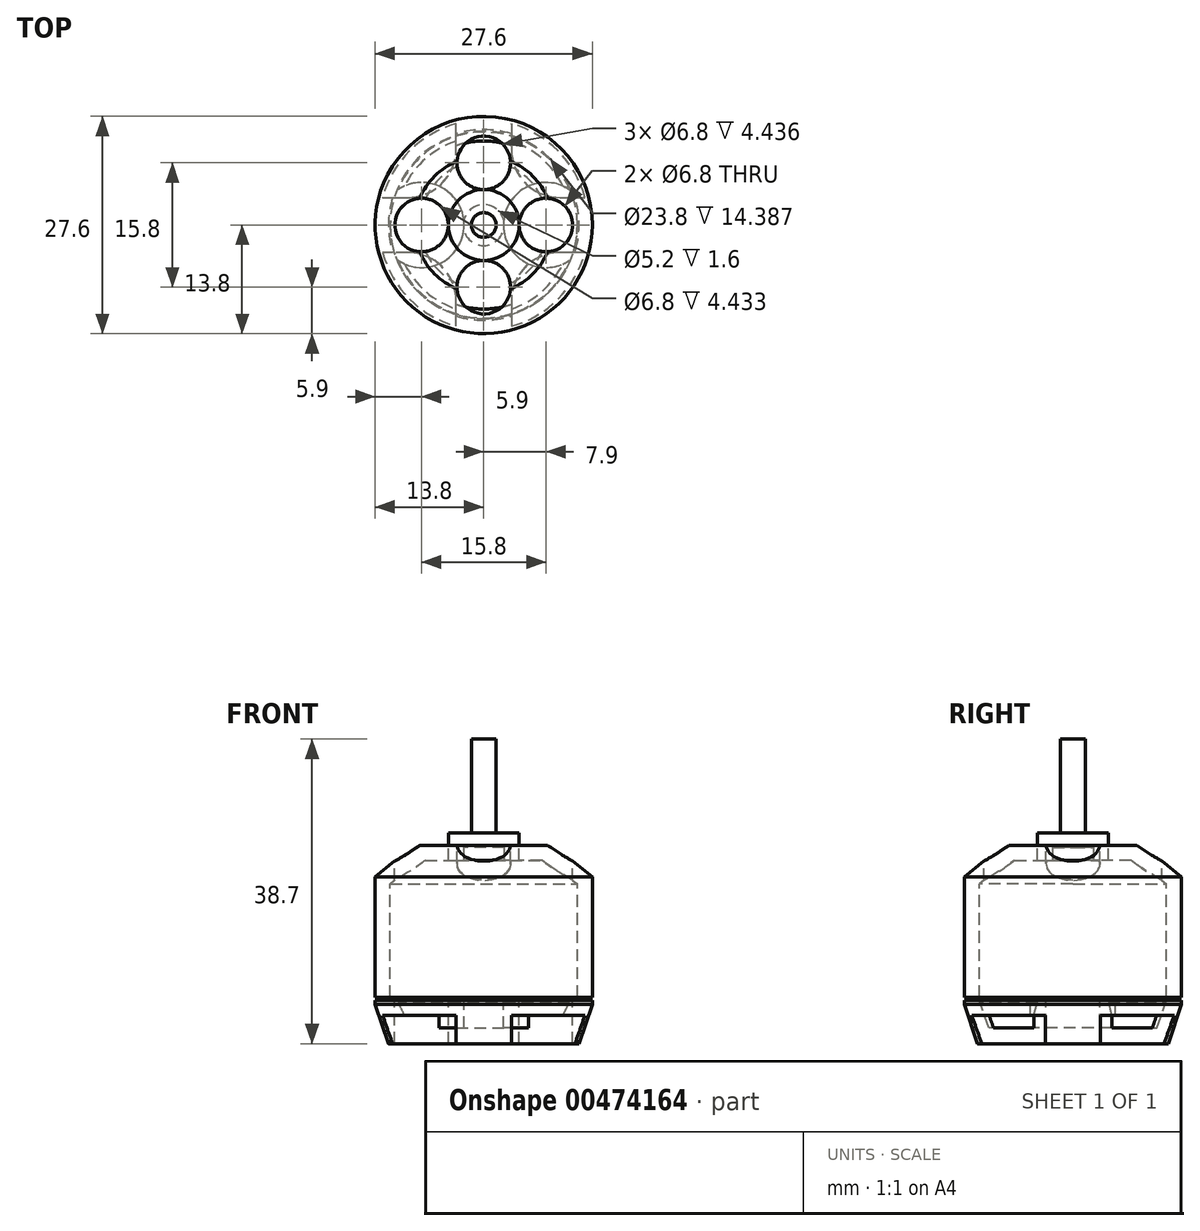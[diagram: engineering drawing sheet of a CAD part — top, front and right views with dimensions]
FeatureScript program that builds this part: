
annotation { "Feature Type Name" : "Feature", "Feature Type Description" : "" }
export const myFeature = defineFeature(function(context is Context, id is Id, definition is map)
    precondition{}
    {
        {
            var Q0;
            Q0=qCreatedBy(makeId("Top.planeOp"),FACE);
            var sketch = newSketch(context, id + "F0", { "sketchPlane" : qUnion([Q0])});
            skCircle(sketch, "E0", {"center": v(0, 0) * mm, "radius": 13.8 * mm});
            skCircle(sketch, "E1", {"center": v(0, 0) * mm, "radius": 1.57 * mm});
            skCircle(sketch, "E2", {"center": v(0, 0) * mm, "radius": 4.5 * mm});
            skCircle(sketch, "E3", {"center": v(0, 0) * mm, "radius": 8.78 * mm});
            skCircle(sketch, "E4", {"center": v(7.9, 0) * mm, "radius": 3.4 * mm});
            skCircle(sketch, "E5.1.0", {"center": v(0, 7.9) * mm, "radius": 3.4 * mm});
            skCircle(sketch, "E5.2.0", {"center": v(-7.9, 0) * mm, "radius": 3.4 * mm});
            skCircle(sketch, "E5.3.0", {"center": v(0, -7.9) * mm, "radius": 3.4 * mm});
            skSolve(sketch);
        }
        {
            var Q0;
            Q0=makeQuery(id+"F0.imprint","IMPRINT",FACE,{"disambiguationData":[TD([[makeQuery(id+"F0.imprint","IMPRINT",EDGE,{"derivedFrom":sQuery(id+"F0.wireOp",EDGE,"E0")}),1.0]])]});
            var Q1;
            {var subQ0=sQuery(id+"F0.wireOp",EDGE,"E5.1.0");var subQ1=sQuery(id+"F0.wireOp",EDGE,"E2");var subQ2=makeQuery(id+"F0.imprint","INTERSECT",VERTEX,{"derivedFrom":[subQ1,subQ0]});Q1=makeQuery(id+"F0.imprint","IMPRINT",FACE,{"disambiguationData":[TD([[makeQuery(id+"F0.imprint","IMPRINT",EDGE,{"disambiguationData":[TD([[subQ2,1.0]])],"derivedFrom":subQ1}),-1.0]])]});}
            var Q2;
            {var subQ0=sQuery(id+"F0.wireOp",EDGE,"E5.1.0");var subQ1=sQuery(id+"F0.wireOp",EDGE,"E2");var subQ2=makeQuery(id+"F0.imprint","INTERSECT",VERTEX,{"derivedFrom":[subQ1,subQ0]});Q2=makeQuery(id+"F0.imprint","IMPRINT",FACE,{"disambiguationData":[TD([[makeQuery(id+"F0.imprint","IMPRINT",EDGE,{"disambiguationData":[TD([[subQ2,-1.0]])],"derivedFrom":subQ1}),-1.0]])]});}
            var Q3;
            Q3=makeQuery(id+"F0.imprint","IMPRINT",FACE,{"disambiguationData":[TD([[makeQuery(id+"F0.imprint","IMPRINT",EDGE,{"derivedFrom":sQuery(id+"F0.wireOp",EDGE,"E1")}),-1.0]])]});
            var Q4;
            {var subQ0=sQuery(id+"F0.wireOp",EDGE,"E4");var subQ1=sQuery(id+"F0.wireOp",EDGE,"E2");var subQ2=makeQuery(id+"F0.imprint","INTERSECT",VERTEX,{"derivedFrom":[subQ1,subQ0]});Q4=makeQuery(id+"F0.imprint","IMPRINT",FACE,{"disambiguationData":[TD([[makeQuery(id+"F0.imprint","IMPRINT",EDGE,{"disambiguationData":[TD([[subQ2,1.0]])],"derivedFrom":subQ1}),-1.0]])]});}
            var Q5;
            {var subQ0=sQuery(id+"F0.wireOp",EDGE,"E5.2.0");var subQ1=sQuery(id+"F0.wireOp",EDGE,"E2");var subQ2=makeQuery(id+"F0.imprint","INTERSECT",VERTEX,{"derivedFrom":[subQ1,subQ0]});Q5=makeQuery(id+"F0.imprint","IMPRINT",FACE,{"disambiguationData":[TD([[makeQuery(id+"F0.imprint","IMPRINT",EDGE,{"disambiguationData":[TD([[subQ2,-1.0]])],"derivedFrom":subQ1}),-1.0]])]});}
            var Q6;
            Q6=makeQuery(id+"F0.imprint","IMPRINT",FACE,{"disambiguationData":[TD([[makeQuery(id+"F0.imprint","IMPRINT",EDGE,{"derivedFrom":sQuery(id+"F0.wireOp",EDGE,"E1")}),1.0]])]});
            var Q7;
            {var subQ0=sQuery(id+"F0.wireOp",EDGE,"E5.2.0");var subQ1=sQuery(id+"F0.wireOp",EDGE,"E3");var subQ2=makeQuery(id+"F0.imprint","INTERSECT",VERTEX,{"disambiguationData":[OD(0.0)],"derivedFrom":[subQ1,subQ0]});Q7=makeQuery(id+"F0.imprint","IMPRINT",FACE,{"disambiguationData":[TD([[makeQuery(id+"F0.imprint","IMPRINT",EDGE,{"disambiguationData":[TD([[subQ2,-1.0]])],"derivedFrom":subQ1}),-1.0]])]});}
            var Q8;
            {var subQ0=sQuery(id+"F0.wireOp",EDGE,"E5.2.0");var subQ1=sQuery(id+"F0.wireOp",EDGE,"E3");var subQ2=makeQuery(id+"F0.imprint","INTERSECT",VERTEX,{"disambiguationData":[OD(0.0)],"derivedFrom":[subQ1,subQ0]});Q8=makeQuery(id+"F0.imprint","IMPRINT",FACE,{"disambiguationData":[TD([[makeQuery(id+"F0.imprint","IMPRINT",EDGE,{"disambiguationData":[TD([[subQ2,-1.0]])],"derivedFrom":subQ1}),1.0]])]});}
            var Q9;
            {var subQ0=sQuery(id+"F0.wireOp",EDGE,"E5.1.0");var subQ1=sQuery(id+"F0.wireOp",EDGE,"E3");var subQ2=makeQuery(id+"F0.imprint","INTERSECT",VERTEX,{"disambiguationData":[OD(0.0)],"derivedFrom":[subQ1,subQ0]});Q9=makeQuery(id+"F0.imprint","IMPRINT",FACE,{"disambiguationData":[TD([[makeQuery(id+"F0.imprint","IMPRINT",EDGE,{"disambiguationData":[TD([[subQ2,-1.0]])],"derivedFrom":subQ1}),1.0]])]});}
            var Q10;
            {var subQ0=sQuery(id+"F0.wireOp",EDGE,"E4");var subQ1=sQuery(id+"F0.wireOp",EDGE,"E3");var subQ2=makeQuery(id+"F0.imprint","INTERSECT",VERTEX,{"disambiguationData":[OD(0.0)],"derivedFrom":[subQ1,subQ0]});Q10=makeQuery(id+"F0.imprint","IMPRINT",FACE,{"disambiguationData":[TD([[makeQuery(id+"F0.imprint","IMPRINT",EDGE,{"disambiguationData":[TD([[subQ2,1.0]])],"derivedFrom":subQ1}),1.0]])]});}
            var Q11;
            {var subQ0=sQuery(id+"F0.wireOp",EDGE,"E4");var subQ1=sQuery(id+"F0.wireOp",EDGE,"E3");var subQ2=makeQuery(id+"F0.imprint","INTERSECT",VERTEX,{"disambiguationData":[OD(0.0)],"derivedFrom":[subQ1,subQ0]});Q11=makeQuery(id+"F0.imprint","IMPRINT",FACE,{"disambiguationData":[TD([[makeQuery(id+"F0.imprint","IMPRINT",EDGE,{"disambiguationData":[TD([[subQ2,1.0]])],"derivedFrom":subQ1}),-1.0]])]});}
            var Q12;
            {var subQ0=sQuery(id+"F0.wireOp",EDGE,"E5.3.0");var subQ1=sQuery(id+"F0.wireOp",EDGE,"E3");var subQ2=makeQuery(id+"F0.imprint","INTERSECT",VERTEX,{"disambiguationData":[OD(0.0)],"derivedFrom":[subQ1,subQ0]});Q12=makeQuery(id+"F0.imprint","IMPRINT",FACE,{"disambiguationData":[TD([[makeQuery(id+"F0.imprint","IMPRINT",EDGE,{"disambiguationData":[TD([[subQ2,-1.0]])],"derivedFrom":subQ1}),1.0]])]});}
            var Q13;
            {var subQ0=sQuery(id+"F0.wireOp",EDGE,"E5.1.0");var subQ1=sQuery(id+"F0.wireOp",EDGE,"E3");var subQ2=makeQuery(id+"F0.imprint","INTERSECT",VERTEX,{"disambiguationData":[OD(0.0)],"derivedFrom":[subQ1,subQ0]});Q13=makeQuery(id+"F0.imprint","IMPRINT",FACE,{"disambiguationData":[TD([[makeQuery(id+"F0.imprint","IMPRINT",EDGE,{"disambiguationData":[TD([[subQ2,-1.0]])],"derivedFrom":subQ1}),-1.0]])]});}
            var Q14;
            {var subQ0=sQuery(id+"F0.wireOp",EDGE,"E5.3.0");var subQ1=sQuery(id+"F0.wireOp",EDGE,"E3");var subQ2=makeQuery(id+"F0.imprint","INTERSECT",VERTEX,{"disambiguationData":[OD(0.0)],"derivedFrom":[subQ1,subQ0]});Q14=makeQuery(id+"F0.imprint","IMPRINT",FACE,{"disambiguationData":[TD([[makeQuery(id+"F0.imprint","IMPRINT",EDGE,{"disambiguationData":[TD([[subQ2,-1.0]])],"derivedFrom":subQ1}),-1.0]])]});}
            extrude(context, id + "F1", {"entities" : qUnion([Q0, Q1, Q2, Q3, Q4, Q5, Q6, Q7, Q8, Q9, Q10, Q11, Q12, Q13, Q14]), "oppositeDirection" : true, "depth" : 19.3 * mm});
        }
        {
            var Q0;
            Q0=makeQuery(id+"F1.opExtrude","CAP_EDGE",EDGE,{"disambiguationData":[OSD([sQuery(id+"F0.wireOp",EDGE,"E0")])],"isStart":true});
            chamfer(context, id + "F2", {"entities" : qUnion([Q0]), "chamferType" : ChamferType.TWO_OFFSETS, "width1" : 5 * mm, "oppositeDirection" : false, "width2" : 4 * mm, "tangentPropagation" : true});
        }
        {
            var Q0;
            Q0=makeQuery(id+"F0.imprint","IMPRINT",FACE,{"disambiguationData":[TD([[makeQuery(id+"F0.imprint","IMPRINT",EDGE,{"derivedFrom":sQuery(id+"F0.wireOp",EDGE,"E1")}),-1.0]])]});
            extrude(context, id + "F3", {"entities" : qUnion([Q0]), "operationType" : NewBodyOperationType.ADD, "depth" : 1.6 * mm});
        }
        {
            var Q0;
            Q0=makeQuery(id+"F0.imprint","IMPRINT",FACE,{"disambiguationData":[TD([[makeQuery(id+"F0.imprint","IMPRINT",EDGE,{"derivedFrom":sQuery(id+"F0.wireOp",EDGE,"E1")}),1.0]])]});
            var Q1;
            Q1=sQuery(id+"F0.wireOp",EDGE,"E1");
            extrude(context, id + "F4", {"entities" : qUnion([Q0]), "operationType" : NewBodyOperationType.ADD, "surfaceEntities" : qUnion([Q1]), "depth" : 13.5 * mm});
        }
        {
            var Q0;
            Q0=makeQuery(id+"F1.opExtrude","CAP_FACE",FACE,{"disambiguationData":[OSD([sQuery(id+"F0.wireOp",EDGE,"E0")])],"isStart":false});
            shell(context, id + "F5", {"entities" : qUnion([Q0]), "thickness" : 1.9 * mm});
        }
        {
            var Q0;
            {var subQ0=sQuery(id+"F0.wireOp",EDGE,"E5.3.0");var subQ1=sQuery(id+"F0.wireOp",EDGE,"E3");var subQ2=makeQuery(id+"F0.imprint","INTERSECT",VERTEX,{"disambiguationData":[OD(0.0)],"derivedFrom":[subQ1,subQ0]});Q0=makeQuery(id+"F0.imprint","IMPRINT",FACE,{"disambiguationData":[TD([[makeQuery(id+"F0.imprint","IMPRINT",EDGE,{"disambiguationData":[TD([[subQ2,-1.0]])],"derivedFrom":subQ1}),-1.0]])]});}
            var Q1;
            {var subQ0=sQuery(id+"F0.wireOp",EDGE,"E5.3.0");var subQ1=sQuery(id+"F0.wireOp",EDGE,"E3");var subQ2=makeQuery(id+"F0.imprint","INTERSECT",VERTEX,{"disambiguationData":[OD(0.0)],"derivedFrom":[subQ1,subQ0]});Q1=makeQuery(id+"F0.imprint","IMPRINT",FACE,{"disambiguationData":[TD([[makeQuery(id+"F0.imprint","IMPRINT",EDGE,{"disambiguationData":[TD([[subQ2,-1.0]])],"derivedFrom":subQ1}),1.0]])]});}
            var Q2;
            {var subQ0=sQuery(id+"F0.wireOp",EDGE,"E4");var subQ1=sQuery(id+"F0.wireOp",EDGE,"E3");var subQ2=makeQuery(id+"F0.imprint","INTERSECT",VERTEX,{"disambiguationData":[OD(0.0)],"derivedFrom":[subQ1,subQ0]});Q2=makeQuery(id+"F0.imprint","IMPRINT",FACE,{"disambiguationData":[TD([[makeQuery(id+"F0.imprint","IMPRINT",EDGE,{"disambiguationData":[TD([[subQ2,1.0]])],"derivedFrom":subQ1}),-1.0]])]});}
            var Q3;
            {var subQ0=sQuery(id+"F0.wireOp",EDGE,"E4");var subQ1=sQuery(id+"F0.wireOp",EDGE,"E3");var subQ2=makeQuery(id+"F0.imprint","INTERSECT",VERTEX,{"disambiguationData":[OD(0.0)],"derivedFrom":[subQ1,subQ0]});Q3=makeQuery(id+"F0.imprint","IMPRINT",FACE,{"disambiguationData":[TD([[makeQuery(id+"F0.imprint","IMPRINT",EDGE,{"disambiguationData":[TD([[subQ2,1.0]])],"derivedFrom":subQ1}),1.0]])]});}
            var Q4;
            {var subQ0=sQuery(id+"F0.wireOp",EDGE,"E5.1.0");var subQ1=sQuery(id+"F0.wireOp",EDGE,"E3");var subQ2=makeQuery(id+"F0.imprint","INTERSECT",VERTEX,{"disambiguationData":[OD(0.0)],"derivedFrom":[subQ1,subQ0]});Q4=makeQuery(id+"F0.imprint","IMPRINT",FACE,{"disambiguationData":[TD([[makeQuery(id+"F0.imprint","IMPRINT",EDGE,{"disambiguationData":[TD([[subQ2,-1.0]])],"derivedFrom":subQ1}),1.0]])]});}
            var Q5;
            {var subQ0=sQuery(id+"F0.wireOp",EDGE,"E5.1.0");var subQ1=sQuery(id+"F0.wireOp",EDGE,"E3");var subQ2=makeQuery(id+"F0.imprint","INTERSECT",VERTEX,{"disambiguationData":[OD(0.0)],"derivedFrom":[subQ1,subQ0]});Q5=makeQuery(id+"F0.imprint","IMPRINT",FACE,{"disambiguationData":[TD([[makeQuery(id+"F0.imprint","IMPRINT",EDGE,{"disambiguationData":[TD([[subQ2,-1.0]])],"derivedFrom":subQ1}),-1.0]])]});}
            var Q6;
            {var subQ0=sQuery(id+"F0.wireOp",EDGE,"E5.2.0");var subQ1=sQuery(id+"F0.wireOp",EDGE,"E3");var subQ2=makeQuery(id+"F0.imprint","INTERSECT",VERTEX,{"disambiguationData":[OD(0.0)],"derivedFrom":[subQ1,subQ0]});Q6=makeQuery(id+"F0.imprint","IMPRINT",FACE,{"disambiguationData":[TD([[makeQuery(id+"F0.imprint","IMPRINT",EDGE,{"disambiguationData":[TD([[subQ2,-1.0]])],"derivedFrom":subQ1}),1.0]])]});}
            var Q7;
            {var subQ0=sQuery(id+"F0.wireOp",EDGE,"E5.2.0");var subQ1=sQuery(id+"F0.wireOp",EDGE,"E3");var subQ2=makeQuery(id+"F0.imprint","INTERSECT",VERTEX,{"disambiguationData":[OD(0.0)],"derivedFrom":[subQ1,subQ0]});Q7=makeQuery(id+"F0.imprint","IMPRINT",FACE,{"disambiguationData":[TD([[makeQuery(id+"F0.imprint","IMPRINT",EDGE,{"disambiguationData":[TD([[subQ2,-1.0]])],"derivedFrom":subQ1}),-1.0]])]});}
            var Q8;
            Q8=sQuery(id+"F0.wireOp",EDGE,"E5.3.0");
            extrude(context, id + "F6", {"entities" : qUnion([Q0, Q1, Q2, Q3, Q4, Q5, Q6, Q7]), "operationType" : NewBodyOperationType.REMOVE, "surfaceEntities" : qUnion([Q8]), "endBound" : BoundingType.THROUGH_ALL, "oppositeDirection" : true, "depth" : 25 * mm});
        }
        {
            var Q0;
            Q0=qCreatedBy(makeId("Top.planeOp"),FACE);
            var sketch = newSketch(context, id + "F7", { "sketchPlane" : qUnion([Q0])});
            skCircle(sketch, "E6", {"center": v(16.95, 0) * mm, "radius": 3.5 * mm});
            skCircle(sketch, "E7.1.0", {"center": v(0, 16.95) * mm, "radius": 3.5 * mm});
            skCircle(sketch, "E7.2.0", {"center": v(-16.95, 0) * mm, "radius": 3.5 * mm});
            skCircle(sketch, "E7.3.0", {"center": v(0, -16.95) * mm, "radius": 3.5 * mm});
            skPoint(sketch, "E7.center", {"position": v(0, 0) * mm});
            skLineSegment(sketch, "E8", {"start": v(16.95, 3.5) * mm, "end": v(9.66, 3.5) * mm});
            skLineSegment(sketch, "E9", {"start": v(3.5, 9.66) * mm, "end": v(3.5, 16.95) * mm});
            skPoint(sketch, "E10.visualSharp", {"position": v(3.5, 3.5) * mm});
            skArc(sketch, "E10.filletArc", {"start": v(3.5, 9.66) * mm, "mid": v(5.3, 5.3) * mm, "end": v(9.66, 3.5) * mm});
            skLineSegment(sketch, "E11.1.0", {"start": v(-3.5, 16.95) * mm, "end": v(-3.5, 9.66) * mm});
            skArc(sketch, "E11.1.1", {"start": v(-9.66, 3.5) * mm, "mid": v(-5.3, 5.3) * mm, "end": v(-3.5, 9.66) * mm});
            skLineSegment(sketch, "E11.1.2", {"start": v(-9.66, 3.5) * mm, "end": v(-16.95, 3.5) * mm});
            skLineSegment(sketch, "E11.2.0", {"start": v(-16.95, -3.5) * mm, "end": v(-9.66, -3.5) * mm});
            skArc(sketch, "E11.2.1", {"start": v(-3.5, -9.66) * mm, "mid": v(-5.3, -5.3) * mm, "end": v(-9.66, -3.5) * mm});
            skLineSegment(sketch, "E11.2.2", {"start": v(-3.5, -9.66) * mm, "end": v(-3.5, -16.95) * mm});
            skLineSegment(sketch, "E11.3.0", {"start": v(3.5, -16.95) * mm, "end": v(3.5, -9.66) * mm});
            skArc(sketch, "E11.3.1", {"start": v(9.66, -3.5) * mm, "mid": v(5.3, -5.3) * mm, "end": v(3.5, -9.66) * mm});
            skLineSegment(sketch, "E11.3.2", {"start": v(9.66, -3.5) * mm, "end": v(16.95, -3.5) * mm});
            skSolve(sketch);
        }
        {
            var Q0;
            Q0=makeQuery(id+"F1.opExtrude","CAP_FACE",FACE,{"disambiguationData":[OSD([sQuery(id+"F0.wireOp",EDGE,"E0")])],"isStart":false});
            cPlane(context, id + "F8", {"entities" : qUnion([Q0]), "cplaneType" : CPlaneType.OFFSET, "offset" : .4 * mm, "width" : 150 * mm, "height" : 150 * mm});
        }
        {
            var Q0;
            Q0=qCreatedBy(id+"F8.planeOp",FACE);
            var sketch = newSketch(context, id + "F9", { "sketchPlane" : qUnion([Q0])});
            skCircle(sketch, "E12", {"center": v(0, 0) * mm, "radius": 13.8 * mm});
            skCircle(sketch, "E13", {"center": v(0, 0) * mm, "radius": 1.57 * mm});
            skCircle(sketch, "E14", {"center": v(0, 0) * mm, "radius": 4.5 * mm});
            skCircle(sketch, "E15", {"center": v(0, 0) * mm, "radius": 8.78 * mm});
            skCircle(sketch, "E16", {"center": v(7.9, 0) * mm, "radius": 3.4 * mm});
            skCircle(sketch, "E17.1.0", {"center": v(0, 7.9) * mm, "radius": 3.4 * mm});
            skCircle(sketch, "E17.2.0", {"center": v(-7.9, 0) * mm, "radius": 3.4 * mm});
            skCircle(sketch, "E17.3.0", {"center": v(0, -7.9) * mm, "radius": 3.4 * mm});
            skSolve(sketch);
        }
        {
            var Q0;
            Q0=makeQuery(id+"F9.imprint","IMPRINT",FACE,{"disambiguationData":[TD([[makeQuery(id+"F9.imprint","IMPRINT",EDGE,{"derivedFrom":sQuery(id+"F9.wireOp",EDGE,"E12")}),1.0]])]});
            var Q1;
            {var subQ0=sQuery(id+"F9.wireOp",EDGE,"E17.3.0");var subQ1=sQuery(id+"F9.wireOp",EDGE,"E15");var subQ2=makeQuery(id+"F9.imprint","INTERSECT",VERTEX,{"disambiguationData":[OD(0.0)],"derivedFrom":[subQ1,subQ0]});Q1=makeQuery(id+"F9.imprint","IMPRINT",FACE,{"disambiguationData":[TD([[makeQuery(id+"F9.imprint","IMPRINT",EDGE,{"disambiguationData":[TD([[subQ2,-1.0]])],"derivedFrom":subQ1}),-1.0]])]});}
            var Q2;
            {var subQ0=sQuery(id+"F9.wireOp",EDGE,"E17.3.0");var subQ1=sQuery(id+"F9.wireOp",EDGE,"E15");var subQ2=makeQuery(id+"F9.imprint","INTERSECT",VERTEX,{"disambiguationData":[OD(0.0)],"derivedFrom":[subQ1,subQ0]});Q2=makeQuery(id+"F9.imprint","IMPRINT",FACE,{"disambiguationData":[TD([[makeQuery(id+"F9.imprint","IMPRINT",EDGE,{"disambiguationData":[TD([[subQ2,-1.0]])],"derivedFrom":subQ1}),1.0]])]});}
            var Q3;
            {var subQ0=sQuery(id+"F9.wireOp",EDGE,"E17.2.0");var subQ1=sQuery(id+"F9.wireOp",EDGE,"E15");var subQ2=makeQuery(id+"F9.imprint","INTERSECT",VERTEX,{"disambiguationData":[OD(0.0)],"derivedFrom":[subQ1,subQ0]});Q3=makeQuery(id+"F9.imprint","IMPRINT",FACE,{"disambiguationData":[TD([[makeQuery(id+"F9.imprint","IMPRINT",EDGE,{"disambiguationData":[TD([[subQ2,-1.0]])],"derivedFrom":subQ1}),-1.0]])]});}
            var Q4;
            {var subQ0=sQuery(id+"F9.wireOp",EDGE,"E17.2.0");var subQ1=sQuery(id+"F9.wireOp",EDGE,"E15");var subQ2=makeQuery(id+"F9.imprint","INTERSECT",VERTEX,{"disambiguationData":[OD(0.0)],"derivedFrom":[subQ1,subQ0]});Q4=makeQuery(id+"F9.imprint","IMPRINT",FACE,{"disambiguationData":[TD([[makeQuery(id+"F9.imprint","IMPRINT",EDGE,{"disambiguationData":[TD([[subQ2,-1.0]])],"derivedFrom":subQ1}),1.0]])]});}
            var Q5;
            {var subQ0=sQuery(id+"F9.wireOp",EDGE,"E17.1.0");var subQ1=sQuery(id+"F9.wireOp",EDGE,"E14");var subQ2=makeQuery(id+"F9.imprint","INTERSECT",VERTEX,{"derivedFrom":[subQ1,subQ0]});Q5=makeQuery(id+"F9.imprint","IMPRINT",FACE,{"disambiguationData":[TD([[makeQuery(id+"F9.imprint","IMPRINT",EDGE,{"disambiguationData":[TD([[subQ2,-1.0]])],"derivedFrom":subQ1}),-1.0]])]});}
            var Q6;
            {var subQ0=sQuery(id+"F9.wireOp",EDGE,"E17.2.0");var subQ1=sQuery(id+"F9.wireOp",EDGE,"E14");var subQ2=makeQuery(id+"F9.imprint","INTERSECT",VERTEX,{"derivedFrom":[subQ1,subQ0]});Q6=makeQuery(id+"F9.imprint","IMPRINT",FACE,{"disambiguationData":[TD([[makeQuery(id+"F9.imprint","IMPRINT",EDGE,{"disambiguationData":[TD([[subQ2,-1.0]])],"derivedFrom":subQ1}),-1.0]])]});}
            var Q7;
            Q7=makeQuery(id+"F9.imprint","IMPRINT",FACE,{"disambiguationData":[TD([[makeQuery(id+"F9.imprint","IMPRINT",EDGE,{"derivedFrom":sQuery(id+"F9.wireOp",EDGE,"E13")}),-1.0]])]});
            var Q8;
            Q8=makeQuery(id+"F9.imprint","IMPRINT",FACE,{"disambiguationData":[TD([[makeQuery(id+"F9.imprint","IMPRINT",EDGE,{"derivedFrom":sQuery(id+"F9.wireOp",EDGE,"E13")}),1.0]])]});
            var Q9;
            {var subQ0=sQuery(id+"F9.wireOp",EDGE,"E16");var subQ1=sQuery(id+"F9.wireOp",EDGE,"E14");var subQ2=makeQuery(id+"F9.imprint","INTERSECT",VERTEX,{"derivedFrom":[subQ1,subQ0]});Q9=makeQuery(id+"F9.imprint","IMPRINT",FACE,{"disambiguationData":[TD([[makeQuery(id+"F9.imprint","IMPRINT",EDGE,{"disambiguationData":[TD([[subQ2,1.0]])],"derivedFrom":subQ1}),-1.0]])]});}
            var Q10;
            {var subQ0=sQuery(id+"F9.wireOp",EDGE,"E16");var subQ1=sQuery(id+"F9.wireOp",EDGE,"E15");var subQ2=makeQuery(id+"F9.imprint","INTERSECT",VERTEX,{"disambiguationData":[OD(0.0)],"derivedFrom":[subQ1,subQ0]});Q10=makeQuery(id+"F9.imprint","IMPRINT",FACE,{"disambiguationData":[TD([[makeQuery(id+"F9.imprint","IMPRINT",EDGE,{"disambiguationData":[TD([[subQ2,1.0]])],"derivedFrom":subQ1}),1.0]])]});}
            var Q11;
            {var subQ0=sQuery(id+"F9.wireOp",EDGE,"E16");var subQ1=sQuery(id+"F9.wireOp",EDGE,"E15");var subQ2=makeQuery(id+"F9.imprint","INTERSECT",VERTEX,{"disambiguationData":[OD(0.0)],"derivedFrom":[subQ1,subQ0]});Q11=makeQuery(id+"F9.imprint","IMPRINT",FACE,{"disambiguationData":[TD([[makeQuery(id+"F9.imprint","IMPRINT",EDGE,{"disambiguationData":[TD([[subQ2,1.0]])],"derivedFrom":subQ1}),-1.0]])]});}
            var Q12;
            {var subQ0=sQuery(id+"F9.wireOp",EDGE,"E17.1.0");var subQ1=sQuery(id+"F9.wireOp",EDGE,"E14");var subQ2=makeQuery(id+"F9.imprint","INTERSECT",VERTEX,{"derivedFrom":[subQ1,subQ0]});Q12=makeQuery(id+"F9.imprint","IMPRINT",FACE,{"disambiguationData":[TD([[makeQuery(id+"F9.imprint","IMPRINT",EDGE,{"disambiguationData":[TD([[subQ2,1.0]])],"derivedFrom":subQ1}),-1.0]])]});}
            var Q13;
            {var subQ0=sQuery(id+"F9.wireOp",EDGE,"E17.1.0");var subQ1=sQuery(id+"F9.wireOp",EDGE,"E15");var subQ2=makeQuery(id+"F9.imprint","INTERSECT",VERTEX,{"disambiguationData":[OD(0.0)],"derivedFrom":[subQ1,subQ0]});Q13=makeQuery(id+"F9.imprint","IMPRINT",FACE,{"disambiguationData":[TD([[makeQuery(id+"F9.imprint","IMPRINT",EDGE,{"disambiguationData":[TD([[subQ2,-1.0]])],"derivedFrom":subQ1}),1.0]])]});}
            var Q14;
            {var subQ0=sQuery(id+"F9.wireOp",EDGE,"E17.1.0");var subQ1=sQuery(id+"F9.wireOp",EDGE,"E15");var subQ2=makeQuery(id+"F9.imprint","INTERSECT",VERTEX,{"disambiguationData":[OD(0.0)],"derivedFrom":[subQ1,subQ0]});Q14=makeQuery(id+"F9.imprint","IMPRINT",FACE,{"disambiguationData":[TD([[makeQuery(id+"F9.imprint","IMPRINT",EDGE,{"disambiguationData":[TD([[subQ2,-1.0]])],"derivedFrom":subQ1}),-1.0]])]});}
            extrude(context, id + "F10", {"entities" : qUnion([Q0, Q1, Q2, Q3, Q4, Q5, Q6, Q7, Q8, Q9, Q10, Q11, Q12, Q13, Q14]), "operationType" : NewBodyOperationType.ADD, "depth" : 5.5 * mm});
        }
        {
            var Q0;
            Q0=makeQuery(id+"F10.opExtrude","CAP_EDGE",EDGE,{"disambiguationData":[OSD([sQuery(id+"F9.wireOp",EDGE,"E12")])],"isStart":false});
            chamfer(context, id + "F11", {"entities" : qUnion([Q0]), "chamferType" : ChamferType.TWO_OFFSETS, "width1" : 5 * mm, "oppositeDirection" : true, "width2" : 1.7 * mm, "tangentPropagation" : true});
        }
        {
            var Q0;
            Q0=makeQuery(id+"F10.opExtrude","CAP_FACE",FACE,{"disambiguationData":[OSD([sQuery(id+"F9.wireOp",EDGE,"E12")])],"isStart":true});
            shell(context, id + "F12", {"entities" : qUnion([Q0]), "thickness" : 2 * mm});
        }
        {
            var Q0;
            Q0=makeQuery(id+"F10.opExtrude","CAP_FACE",FACE,{"disambiguationData":[OSD([sQuery(id+"F9.wireOp",EDGE,"E12")])],"isStart":false});
            cPlane(context, id + "F13", {"entities" : qUnion([Q0]), "cplaneType" : CPlaneType.OFFSET, "offset" : 0 * mm, "width" : 150 * mm, "height" : 150 * mm});
        }
        {
            var Q0;
            Q0=qCreatedBy(id+"F13.planeOp",FACE);
            var sketch = newSketch(context, id + "F14", { "sketchPlane" : qUnion([Q0])});
            skCircle(sketch, "E18", {"center": v(16.95, 0) * mm, "radius": 3.5 * mm});
            skCircle(sketch, "E19.1.0", {"center": v(0, 16.95) * mm, "radius": 3.5 * mm});
            skCircle(sketch, "E19.2.0", {"center": v(-16.95, 0) * mm, "radius": 3.5 * mm});
            skCircle(sketch, "E19.3.0", {"center": v(0, -16.95) * mm, "radius": 3.5 * mm});
            skPoint(sketch, "E19.center", {"position": v(0, 0) * mm});
            skLineSegment(sketch, "E20", {"start": v(16.95, 3.5) * mm, "end": v(9.66, 3.5) * mm});
            skLineSegment(sketch, "E21", {"start": v(3.5, 9.66) * mm, "end": v(3.5, 16.95) * mm});
            skPoint(sketch, "E22.visualSharp", {"position": v(3.5, 3.5) * mm});
            skArc(sketch, "E22.filletArc", {"start": v(3.5, 9.66) * mm, "mid": v(5.3, 5.3) * mm, "end": v(9.66, 3.5) * mm});
            skLineSegment(sketch, "E23.1.0", {"start": v(-3.5, 16.95) * mm, "end": v(-3.5, 9.66) * mm});
            skArc(sketch, "E23.1.1", {"start": v(-9.66, 3.5) * mm, "mid": v(-5.3, 5.3) * mm, "end": v(-3.5, 9.66) * mm});
            skLineSegment(sketch, "E23.1.2", {"start": v(-9.66, 3.5) * mm, "end": v(-16.95, 3.5) * mm});
            skLineSegment(sketch, "E23.2.0", {"start": v(-16.95, -3.5) * mm, "end": v(-9.66, -3.5) * mm});
            skArc(sketch, "E23.2.1", {"start": v(-3.5, -9.66) * mm, "mid": v(-5.3, -5.3) * mm, "end": v(-9.66, -3.5) * mm});
            skLineSegment(sketch, "E23.2.2", {"start": v(-3.5, -9.66) * mm, "end": v(-3.5, -16.95) * mm});
            skLineSegment(sketch, "E23.3.0", {"start": v(3.5, -16.95) * mm, "end": v(3.5, -9.66) * mm});
            skArc(sketch, "E23.3.1", {"start": v(9.66, -3.5) * mm, "mid": v(5.3, -5.3) * mm, "end": v(3.5, -9.66) * mm});
            skLineSegment(sketch, "E23.3.2", {"start": v(9.66, -3.5) * mm, "end": v(16.95, -3.5) * mm});
            skCircle(sketch, "E24", {"center": v(0, 0) * mm, "radius": 18.5 * mm});
            skCircle(sketch, "E25", {"center": v(16.95, 0) * mm, "radius": 1.5 * mm});
            skCircle(sketch, "E26.1.0", {"center": v(0, 16.95) * mm, "radius": 1.5 * mm});
            skCircle(sketch, "E26.2.0", {"center": v(-16.95, 0) * mm, "radius": 1.5 * mm});
            skCircle(sketch, "E26.3.0", {"center": v(0, -16.95) * mm, "radius": 1.5 * mm});
            skSolve(sketch);
        }
        {
            var Q0;
            {var subQ0=sQuery(id+"F14.wireOp",EDGE,"E23.1.1");Q0=makeQuery(id+"F14.imprint","IMPRINT",FACE,{"disambiguationData":[TD([[makeQuery(id+"F14.imprint","IMPRINT",EDGE,{"derivedFrom":subQ0}),1.0]])]});}
            var Q1;
            {var subQ0=sQuery(id+"F14.wireOp",EDGE,"E22.filletArc");Q1=makeQuery(id+"F14.imprint","IMPRINT",FACE,{"disambiguationData":[TD([[makeQuery(id+"F14.imprint","IMPRINT",EDGE,{"derivedFrom":subQ0}),1.0]])]});}
            var Q2;
            {var subQ0=sQuery(id+"F14.wireOp",EDGE,"E23.3.1");Q2=makeQuery(id+"F14.imprint","IMPRINT",FACE,{"disambiguationData":[TD([[makeQuery(id+"F14.imprint","IMPRINT",EDGE,{"derivedFrom":subQ0}),1.0]])]});}
            var Q3;
            {var subQ0=sQuery(id+"F14.wireOp",EDGE,"E23.2.1");Q3=makeQuery(id+"F14.imprint","IMPRINT",FACE,{"disambiguationData":[TD([[makeQuery(id+"F14.imprint","IMPRINT",EDGE,{"derivedFrom":subQ0}),1.0]])]});}
            extrude(context, id + "F15", {"entities" : qUnion([Q0, Q1, Q2, Q3]), "operationType" : NewBodyOperationType.REMOVE, "oppositeDirection" : true, "depth" : 3.6 * mm});
        }
    });
